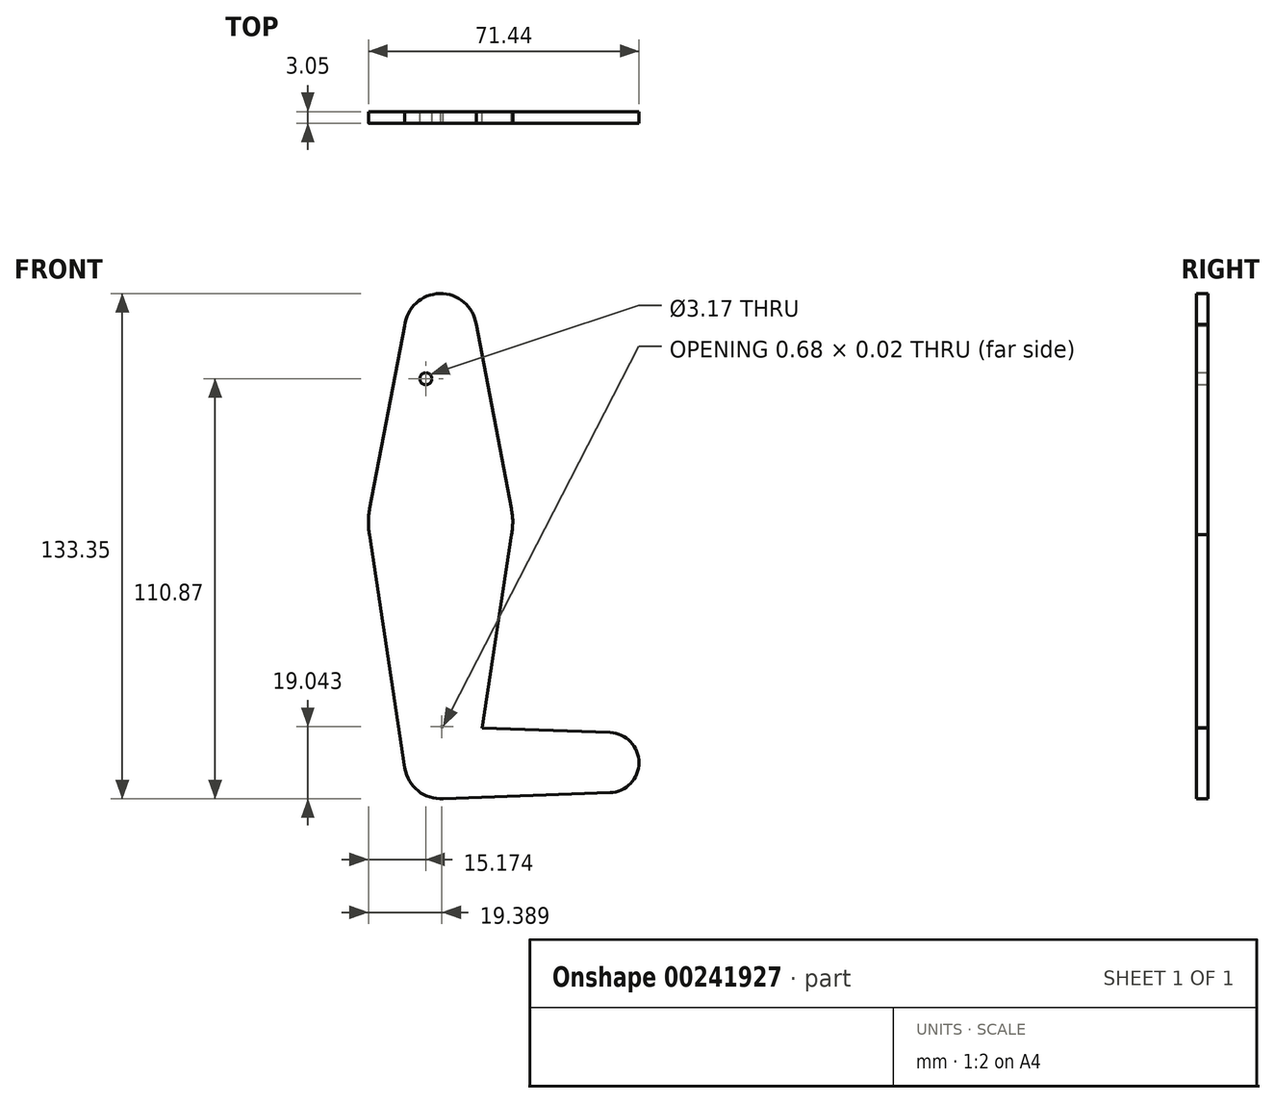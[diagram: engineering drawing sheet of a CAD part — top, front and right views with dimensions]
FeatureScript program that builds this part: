
annotation { "Feature Type Name" : "Feature", "Feature Type Description" : "" }
export const myFeature = defineFeature(function(context is Context, id is Id, definition is map)
    precondition{}
    {
        {
            var Q0;
            Q0=qCreatedBy(makeId("Front.planeOp"),FACE);
            var sketch = newSketch(context, id + "F0", { "sketchPlane" : qUnion([Q0])});
            skCircle(sketch, "E0", {"center": v(44.45, -37.3) * mm, "radius": 7.94 * mm});
            skCircle(sketch, "E1", {"center": v(0, -37.3) * mm, "radius": 9.53 * mm});
            skCircle(sketch, "E2", {"center": v(0, 77) * mm, "radius": 9.53 * mm});
            skCircle(sketch, "E3", {"center": v(0, 26.2) * mm, "radius": 19.05 * mm});
            skLineSegment(sketch, "E4", {"start": v(-18.9, 23.82) * mm, "end": v(-9.42, -38.72) * mm});
            skLineSegment(sketch, "E5", {"start": v(-9.47, 78.05) * mm, "end": v(-18.7, 29.8) * mm});
            skLineSegment(sketch, "E6", {"start": v(18.9, 23.82) * mm, "end": v(9.42, -38.72) * mm});
            skLineSegment(sketch, "E7", {"start": v(9.42, 78.44) * mm, "end": v(18.71, 29.78) * mm});
            skLineSegment(sketch, "E8", {"start": v(0, -27.77) * mm, "end": v(44.73, -29.36) * mm});
            skLineSegment(sketch, "E9", {"start": v(0, -46.82) * mm, "end": v(44.73, -45.22) * mm});
            skCircle(sketch, "E10", {"center": v(-3.88, 64.05) * mm, "radius": 1.59 * mm});
            skSolve(sketch);
        }
        {
            var Q0;
            Q0 = qSketchRegion(id + "F0", true);
            extrude(context, id + "F1", {"entities" : qUnion([Q0]), "depth" : 3.05 * mm});
        }
    });
